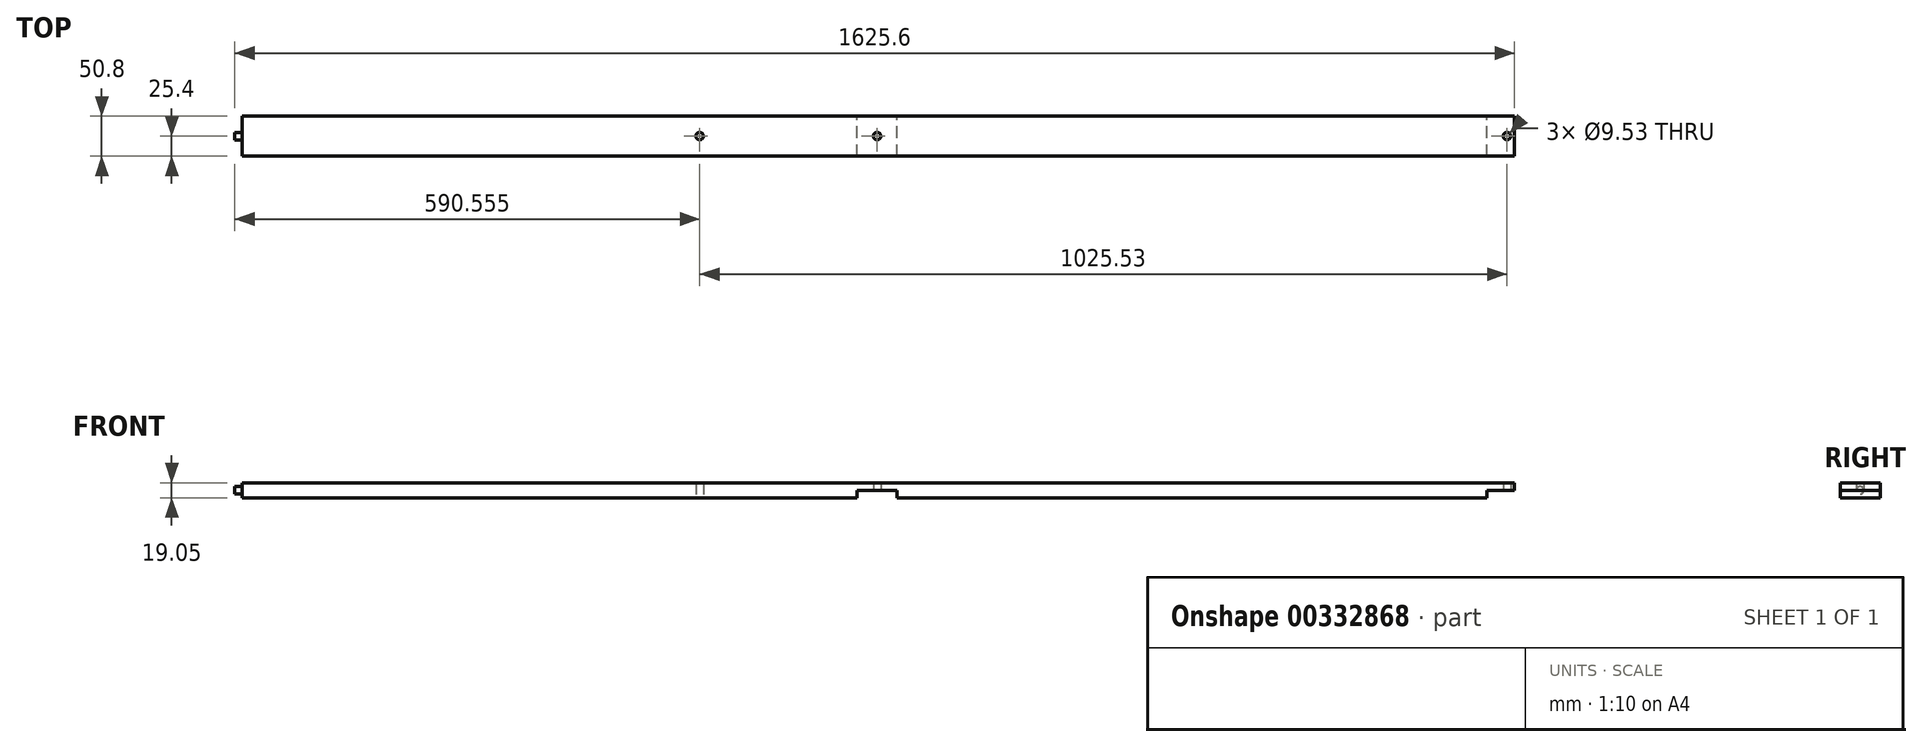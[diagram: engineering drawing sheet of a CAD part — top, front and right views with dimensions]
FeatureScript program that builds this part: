
annotation { "Feature Type Name" : "Feature", "Feature Type Description" : "" }
export const myFeature = defineFeature(function(context is Context, id is Id, definition is map)
    precondition{}
    {
        {
            var Q0;
            Q0=qCreatedBy(makeId("Front.planeOp"),FACE);
            var sketch = newSketch(context, id + "F0", { "sketchPlane" : qUnion([Q0])});
            skLineSegment(sketch, "E0", {"start": v(1616.08, 19.05) * mm, "end": v(0, 19.05) * mm});
            skPoint(sketch, "E1.left.start.orphan", {"position": v(-798.41, -3.82) * mm});
            skLineSegment(sketch, "E2.top", {"start": v(781.05, 9.52) * mm, "end": v(831.85, 9.52) * mm});
            skLineSegment(sketch, "E2.left", {"start": v(781.05, 0) * mm, "end": v(781.05, 9.52) * mm});
            skLineSegment(sketch, "E2.right", {"start": v(831.85, 0) * mm, "end": v(831.85, 9.52) * mm});
            skLineSegment(sketch, "E3.trimOffspring", {"start": v(831.85, 0) * mm, "end": v(1581.15, 0) * mm});
            skLineSegment(sketch, "E4.left", {"start": v(1581.15, 0) * mm, "end": v(1581.15, 9.53) * mm});
            skLineSegment(sketch, "E5.trimOffspring", {"start": v(939.8, 0) * mm, "end": v(939.8, 0) * mm});
            skLineSegment(sketch, "E6.top", {"start": v(1581.15, 9.52) * mm, "end": v(1616.08, 9.52) * mm});
            skPoint(sketch, "E7.orphan", {"position": v(1631.95, 0) * mm});
            skLineSegment(sketch, "E8", {"start": v(0, 0) * mm, "end": v(0, 19.05) * mm});
            skLineSegment(sketch, "E9", {"start": v(781.05, 0) * mm, "end": v(0, 0) * mm});
            skLineSegment(sketch, "E10", {"start": v(1616.08, 19.05) * mm, "end": v(1616.08, 9.53) * mm});
            skSolve(sketch);
        }
        {
            var Q0;
            Q0=qSketchRegion(id+"F0",true);
            extrude(context, id + "F1", {"entities" : qUnion([Q0]), "depth" : 50.8 * mm});
        }
        {
            var Q0;
            Q0=qCreatedBy(makeId("Top.planeOp"),FACE);
            cPlane(context, id + "F2", {"entities" : qUnion([Q0]), "cplaneType" : CPlaneType.OFFSET, "offset" : 9.52 * mm, "width" : 152.4 * mm, "height" : 152.4 * mm});
        }
        {
            var Q0;
            Q0=qCreatedBy(id+"F2.planeOp",FACE);
            var sketch = newSketch(context, id + "F3", { "sketchPlane" : qUnion([Q0])});
            skCircle(sketch, "E11", {"center": v(806.45, -25.4) * mm, "radius": 4.76 * mm});
            skCircle(sketch, "E12", {"center": v(1606.55, -25.4) * mm, "radius": 4.76 * mm});
            skCircle(sketch, "E13", {"center": v(581.02, -25.4) * mm, "radius": 4.76 * mm});
            skSolve(sketch);
        }
        {
            var Q0;
            Q0=qSketchRegion(id+"F3",true);
            extrude(context, id + "F4", {"entities" : qUnion([Q0]), "operationType" : NewBodyOperationType.REMOVE, "endBound" : BoundingType.SYMMETRIC, "depth" : 25.4 * mm});
        }
        {
            var Q0;
            Q0=qCreatedBy(makeId("Right.planeOp"),FACE);
            var sketch = newSketch(context, id + "F5", { "sketchPlane" : qUnion([Q0])});
            skCircle(sketch, "E14", {"center": v(-25.4, 9.53) * mm, "radius": 4.76 * mm});
            skSolve(sketch);
        }
        {
            var Q0;
            Q0=qSketchRegion(id+"F5",true);
            extrude(context, id + "F6", {"entities" : qUnion([Q0]), "operationType" : NewBodyOperationType.ADD, "oppositeDirection" : true, "depth" : 9.52 * mm});
        }
    });
